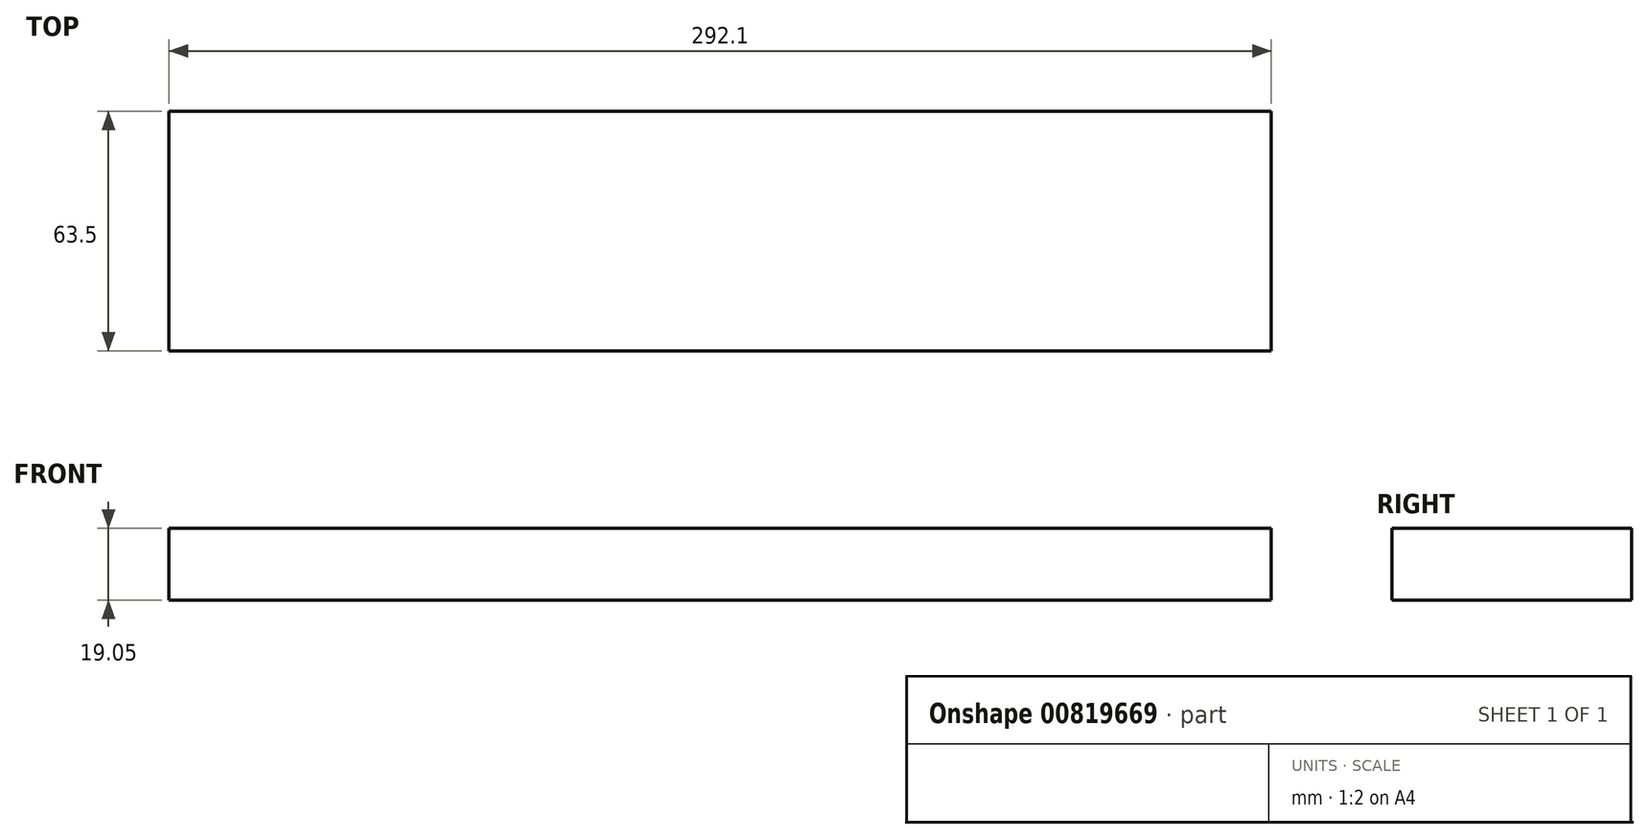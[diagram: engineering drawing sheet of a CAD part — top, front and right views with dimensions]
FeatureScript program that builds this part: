
annotation { "Feature Type Name" : "Feature", "Feature Type Description" : "" }
export const myFeature = defineFeature(function(context is Context, id is Id, definition is map)
    precondition{}
    {
        {
            var Q0;
            Q0=qCreatedBy(makeId("Front.planeOp"),FACE);
            var sketch = newSketch(context, id + "F0", { "sketchPlane" : qUnion([Q0])});
            skLineSegment(sketch, "E0.bottom", {"start": v(224.44, 0) * mm, "end": v(-67.66, 0) * mm});
            skLineSegment(sketch, "E0.top", {"start": v(224.44, 19.05) * mm, "end": v(-67.66, 19.05) * mm});
            skLineSegment(sketch, "E0.left", {"start": v(224.44, 0) * mm, "end": v(224.44, 19.05) * mm});
            skLineSegment(sketch, "E0.right", {"start": v(-67.66, 0) * mm, "end": v(-67.66, 19.05) * mm});
            skSolve(sketch);
        }
        {
            var Q0;
            Q0=qSketchRegion(id+"F0",true);
            extrude(context, id + "F1", {"entities" : qUnion([Q0]), "depth" : 63.5 * mm, "offsetDistance" : 25.4 * mm});
        }
    });
